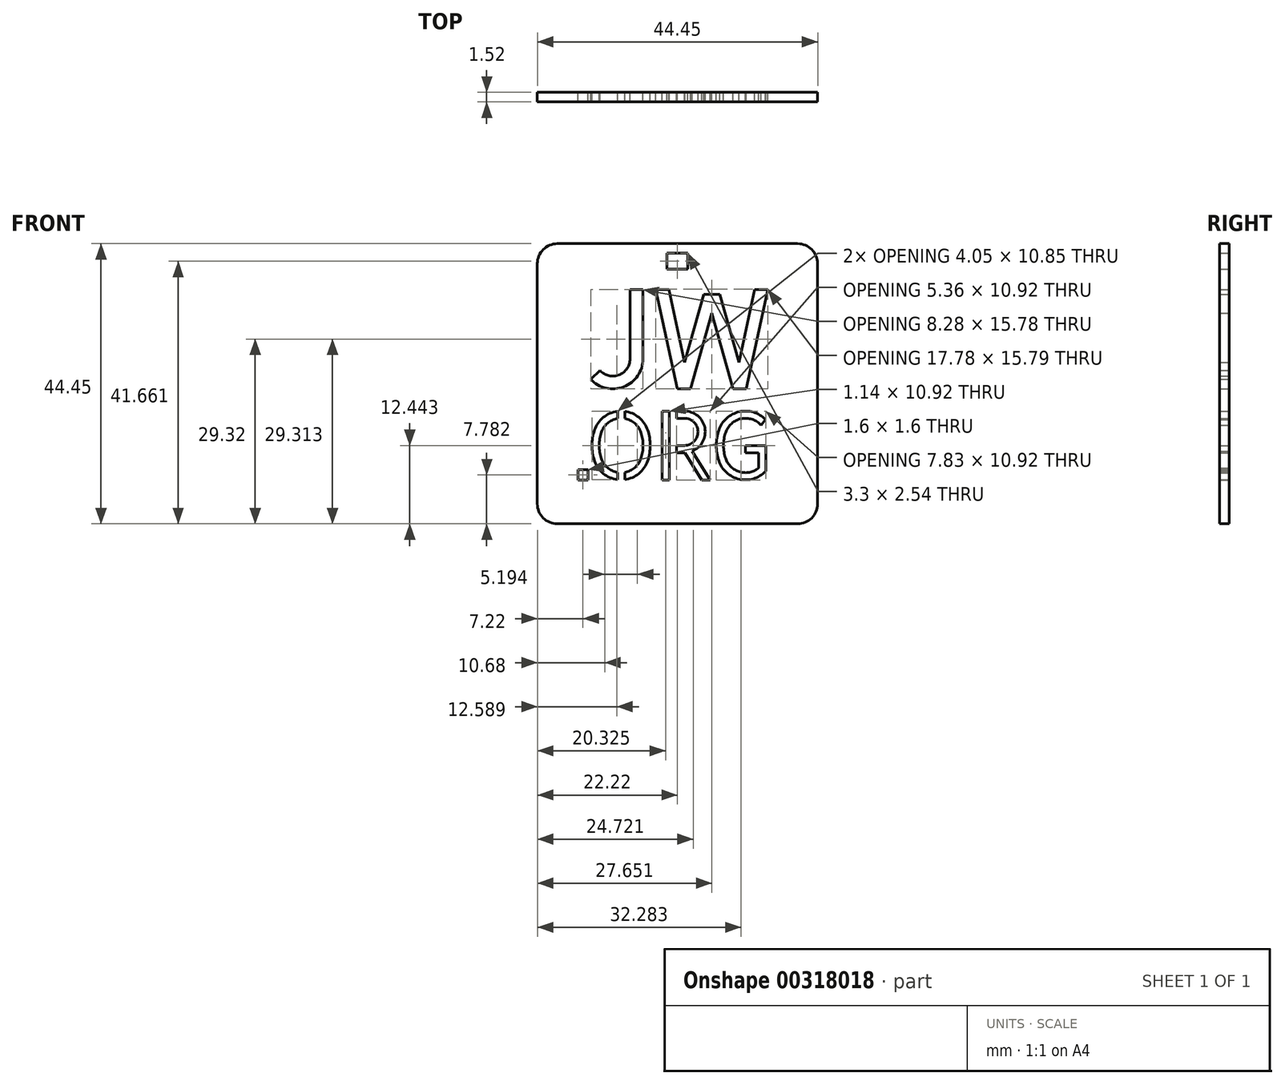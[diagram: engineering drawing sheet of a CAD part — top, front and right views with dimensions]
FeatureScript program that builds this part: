
annotation { "Feature Type Name" : "Feature", "Feature Type Description" : "" }
export const myFeature = defineFeature(function(context is Context, id is Id, definition is map)
    precondition{}
    {
        {
            var Q0;
            Q0=qCreatedBy(makeId("Front.planeOp"),FACE);
            var sketch = newSketch(context, id + "F0", { "sketchPlane" : qUnion([Q0])});
            skPoint(sketch, "E0.0", {"position": v(0, 0) * mm});
            skArc(sketch, "E1.0", {"start": v(-37.67, 27.5) * mm, "mid": v(-34.67, 26.8) * mm, "end": v(-32.92, 29.36) * mm});
            skLineSegment(sketch, "E2.0", {"start": v(-39.17, 26.13) * mm, "end": v(-37.67, 27.5) * mm});
            skArc(sketch, "E3.0", {"start": v(-39.17, 26.13) * mm, "mid": v(-33.93, 24.91) * mm, "end": v(-30.9, 29.36) * mm});
            skLineSegment(sketch, "E4.0", {"start": v(-30.9, 29.36) * mm, "end": v(-30.9, 40.38) * mm});
            skLineSegment(sketch, "E5.0", {"start": v(-32.92, 40.38) * mm, "end": v(-32.92, 29.36) * mm});
            skPoint(sketch, "E6.0", {"position": v(-31.9, 40.38) * mm});
            skPoint(sketch, "E7.0", {"position": v(-27.82, 40.38) * mm});
            skLineSegment(sketch, "E8.0", {"start": v(-21.24, 39.62) * mm, "end": v(-18.7, 39.62) * mm});
            skPoint(sketch, "E9.0", {"position": v(-12.12, 40.38) * mm});
            skLineSegment(sketch, "E10.0", {"start": v(-13.16, 40.38) * mm, "end": v(-11.08, 40.38) * mm});
            skLineSegment(sketch, "E11.0", {"start": v(-28.86, 40.38) * mm, "end": v(-26.78, 40.38) * mm});
            skLineSegment(sketch, "E12.0", {"start": v(-30.9, 40.38) * mm, "end": v(-32.92, 40.38) * mm});
            skLineSegment(sketch, "E13.0", {"start": v(-28.86, 40.38) * mm, "end": v(-25.45, 24.59) * mm});
            skLineSegment(sketch, "E14.0", {"start": v(-26.78, 40.38) * mm, "end": v(-24.28, 28.8) * mm});
            skLineSegment(sketch, "E15.0", {"start": v(-21.24, 39.62) * mm, "end": v(-24.28, 28.8) * mm});
            skLineSegment(sketch, "E16.0", {"start": v(-15.65, 28.8) * mm, "end": v(-18.7, 39.62) * mm});
            skLineSegment(sketch, "E17.0", {"start": v(-15.65, 28.8) * mm, "end": v(-13.16, 40.38) * mm});
            skLineSegment(sketch, "E18.0", {"start": v(-14.48, 24.59) * mm, "end": v(-11.08, 40.38) * mm});
            skLineSegment(sketch, "E19.0", {"start": v(-16.58, 24.59) * mm, "end": v(-14.48, 24.59) * mm});
            skLineSegment(sketch, "E20.0", {"start": v(-16.58, 24.59) * mm, "end": v(-19.97, 36.63) * mm});
            skLineSegment(sketch, "E21.0", {"start": v(-19.97, 36.63) * mm, "end": v(-23.36, 24.59) * mm});
            skLineSegment(sketch, "E22.0", {"start": v(-25.45, 24.59) * mm, "end": v(-23.36, 24.59) * mm});
            skPoint(sketch, "E23", {"position": v(-40.4, 10.95) * mm});
            skPoint(sketch, "E24", {"position": v(-27.87, 10.15) * mm});
            skPoint(sketch, "E25", {"position": v(-34.34, 10.15) * mm});
            skPoint(sketch, "E26", {"position": v(-14.63, 10.15) * mm});
            skLineSegment(sketch, "E27.bottom", {"start": v(-39.6, 11.75) * mm, "end": v(-41.2, 11.75) * mm});
            skLineSegment(sketch, "E27.top", {"start": v(-39.6, 10.15) * mm, "end": v(-41.2, 10.15) * mm});
            skLineSegment(sketch, "E27.left", {"start": v(-39.6, 11.75) * mm, "end": v(-39.6, 10.15) * mm});
            skLineSegment(sketch, "E27.right", {"start": v(-41.2, 11.75) * mm, "end": v(-41.2, 10.15) * mm});
            skArc(sketch, "E28.0", {"start": v(-34.91, 19.88) * mm, "mid": v(-36.5, 19.13) * mm, "end": v(-37.48, 17.68) * mm});
            skArc(sketch, "E28.1", {"start": v(-37.48, 13.55) * mm, "mid": v(-36.5, 12.1) * mm, "end": v(-34.91, 11.34) * mm});
            skArc(sketch, "E28.2", {"start": v(-38.57, 13.18) * mm, "mid": v(-37.17, 11.16) * mm, "end": v(-34.91, 10.19) * mm});
            skArc(sketch, "E28.3", {"start": v(-34.91, 19.88) * mm, "mid": v(-36.5, 19.13) * mm, "end": v(-37.48, 17.68) * mm});
            skArc(sketch, "E28.4", {"start": v(-34.91, 21.04) * mm, "mid": v(-37.17, 20.06) * mm, "end": v(-38.57, 18.04) * mm});
            skArc(sketch, "E28.5", {"start": v(-37.48, 13.55) * mm, "mid": v(-36.5, 12.1) * mm, "end": v(-34.91, 11.34) * mm});
            skArc(sketch, "E28.6", {"start": v(-37.48, 17.68) * mm, "mid": v(-37.82, 15.61) * mm, "end": v(-37.48, 13.55) * mm});
            skArc(sketch, "E28.7", {"start": v(-38.57, 18.04) * mm, "mid": v(-38.97, 15.61) * mm, "end": v(-38.57, 13.18) * mm});
            skArc(sketch, "E28.8", {"start": v(-33.77, 11.34) * mm, "mid": v(-32.19, 12.1) * mm, "end": v(-31.2, 13.55) * mm});
            skArc(sketch, "E28.9", {"start": v(-30.12, 13.18) * mm, "mid": v(-29.72, 15.61) * mm, "end": v(-30.12, 18.04) * mm});
            skArc(sketch, "E28.10", {"start": v(-30.12, 18.04) * mm, "mid": v(-31.52, 20.06) * mm, "end": v(-33.77, 21.04) * mm});
            skArc(sketch, "E28.11", {"start": v(-31.2, 17.68) * mm, "mid": v(-32.19, 19.13) * mm, "end": v(-33.77, 19.88) * mm});
            skArc(sketch, "E28.12", {"start": v(-30.12, 18.04) * mm, "mid": v(-31.52, 20.06) * mm, "end": v(-33.77, 21.04) * mm});
            skArc(sketch, "E28.13", {"start": v(-31.2, 13.55) * mm, "mid": v(-30.86, 15.61) * mm, "end": v(-31.2, 17.68) * mm});
            skArc(sketch, "E28.14", {"start": v(-33.77, 10.19) * mm, "mid": v(-31.52, 11.16) * mm, "end": v(-30.12, 13.18) * mm});
            skArc(sketch, "E28.15", {"start": v(-33.77, 10.19) * mm, "mid": v(-31.52, 11.16) * mm, "end": v(-30.12, 13.18) * mm});
            skLineSegment(sketch, "E29.0", {"start": v(-34.91, 21.04) * mm, "end": v(-34.91, 19.88) * mm});
            skLineSegment(sketch, "E30.0", {"start": v(-33.77, 21.04) * mm, "end": v(-33.77, 19.88) * mm});
            skLineSegment(sketch, "E31.0", {"start": v(-34.91, 11.34) * mm, "end": v(-34.91, 10.19) * mm});
            skLineSegment(sketch, "E32.0", {"start": v(-33.77, 11.34) * mm, "end": v(-33.77, 10.19) * mm});
            skLineSegment(sketch, "E33.0.0", {"start": v(-26.72, 21.07) * mm, "end": v(-26.72, 10.15) * mm});
            skLineSegment(sketch, "E33.0.1", {"start": v(-26.72, 21.07) * mm, "end": v(-27.87, 21.07) * mm});
            skLineSegment(sketch, "E33.0.2", {"start": v(-27.87, 21.07) * mm, "end": v(-27.87, 10.15) * mm});
            skLineSegment(sketch, "E33.0.3", {"start": v(-27.87, 10.15) * mm, "end": v(-26.72, 10.15) * mm});
            skLineSegment(sketch, "E34.0.0", {"start": v(-24.3, 21.07) * mm, "end": v(-25.58, 21.07) * mm});
            skLineSegment(sketch, "E34.0.1", {"start": v(-25.58, 21.07) * mm, "end": v(-25.58, 19.93) * mm});
            skLineSegment(sketch, "E34.0.2", {"start": v(-25.58, 19.93) * mm, "end": v(-24.3, 19.93) * mm});
            skArc(sketch, "E34.0.3", {"start": v(-24.3, 19.93) * mm, "mid": v(-22.15, 17.8) * mm, "end": v(-24.26, 15.61) * mm});
            skLineSegment(sketch, "E34.0.4", {"start": v(-24.26, 15.61) * mm, "end": v(-25.58, 15.61) * mm});
            skLineSegment(sketch, "E34.0.5", {"start": v(-25.58, 15.61) * mm, "end": v(-25.58, 14.47) * mm});
            skFitSpline(sketch, "E34.0.6", {"points": [v(-26.72, 14.47) * mm, v(-25.9, 14.47) * mm, v(-25.08, 14.47) * mm, v(-24.25, 14.47) * mm]});
            skLineSegment(sketch, "E34.0.7", {"start": v(-24.25, 14.47) * mm, "end": v(-21.56, 10.15) * mm});
            skLineSegment(sketch, "E34.0.8", {"start": v(-21.56, 10.15) * mm, "end": v(-20.22, 10.15) * mm});
            skLineSegment(sketch, "E34.0.9", {"start": v(-20.22, 10.15) * mm, "end": v(-23.06, 14.72) * mm});
            skArc(sketch, "E34.0.10", {"start": v(-23.06, 14.72) * mm, "mid": v(-21.07, 18.4) * mm, "end": v(-24.3, 21.07) * mm});
            skArc(sketch, "E35.0.0", {"start": v(-17.77, 17.68) * mm, "mid": v(-15.28, 19.87) * mm, "end": v(-12.14, 18.8) * mm});
            skLineSegment(sketch, "E35.0.1", {"start": v(-12.14, 18.8) * mm, "end": v(-11.43, 19.72) * mm});
            skArc(sketch, "E35.0.2", {"start": v(-11.43, 19.72) * mm, "mid": v(-15.61, 20.96) * mm, "end": v(-18.85, 18.04) * mm});
            skArc(sketch, "E35.0.3", {"start": v(-18.85, 18.04) * mm, "mid": v(-19.25, 15.61) * mm, "end": v(-18.85, 13.18) * mm});
            skArc(sketch, "E35.0.4", {"start": v(-18.85, 13.18) * mm, "mid": v(-15.6, 10.26) * mm, "end": v(-11.42, 11.5) * mm});
            skLineSegment(sketch, "E35.0.5", {"start": v(-11.42, 11.5) * mm, "end": v(-11.42, 15.61) * mm});
            skLineSegment(sketch, "E35.0.6", {"start": v(-11.42, 15.61) * mm, "end": v(-14.63, 15.61) * mm});
            skLineSegment(sketch, "E35.0.7", {"start": v(-14.63, 15.61) * mm, "end": v(-14.63, 14.47) * mm});
            skLineSegment(sketch, "E35.0.8", {"start": v(-14.63, 14.47) * mm, "end": v(-12.57, 14.47) * mm});
            skLineSegment(sketch, "E35.0.9", {"start": v(-12.57, 14.47) * mm, "end": v(-12.57, 12.01) * mm});
            skArc(sketch, "E35.0.10", {"start": v(-12.57, 12.01) * mm, "mid": v(-15.57, 11.43) * mm, "end": v(-17.77, 13.55) * mm});
            skArc(sketch, "E35.0.11", {"start": v(-17.77, 13.55) * mm, "mid": v(-18.1, 15.61) * mm, "end": v(-17.77, 17.68) * mm});
            skSolve(sketch);
        }
        {
            var Q0;
            Q0=qCreatedBy(makeId("Front.planeOp"),FACE);
            var sketch = newSketch(context, id + "F1", { "sketchPlane" : qUnion([Q0])});
            skLineSegment(sketch, "E36.bottom", {"start": v(0, 0) * mm, "end": v(-50.8, 0) * mm});
            skLineSegment(sketch, "E36.top", {"start": v(0, 50.8) * mm, "end": v(-50.8, 50.8) * mm});
            skLineSegment(sketch, "E36.left", {"start": v(0, 0) * mm, "end": v(0, 50.8) * mm});
            skLineSegment(sketch, "E36.right", {"start": v(-50.8, 0) * mm, "end": v(-50.8, 50.8) * mm});
            skLineSegment(sketch, "E37.0", {"start": v(-3.18, 47.63) * mm, "end": v(-47.63, 47.63) * mm});
            skLineSegment(sketch, "E37.1", {"start": v(-3.17, 3.18) * mm, "end": v(-3.18, 47.63) * mm});
            skLineSegment(sketch, "E37.2", {"start": v(-3.17, 3.17) * mm, "end": v(-47.63, 3.17) * mm});
            skLineSegment(sketch, "E37.3", {"start": v(-47.63, 3.17) * mm, "end": v(-47.63, 47.62) * mm});
            skPoint(sketch, "E38.0", {"position": v(-41.2, 10.15) * mm});
            skPoint(sketch, "E39", {"position": v(-25.4, 25.4) * mm});
            skCircle(sketch, "E40", {"center": v(-25.4, 25.4) * mm, "radius": 25.4 * mm});
            skLineSegment(sketch, "E41.bottom", {"start": v(-23.75, 46.1) * mm, "end": v(-27.05, 46.1) * mm});
            skLineSegment(sketch, "E41.top", {"start": v(-23.75, 43.56) * mm, "end": v(-27.05, 43.56) * mm});
            skLineSegment(sketch, "E41.left", {"start": v(-23.75, 46.1) * mm, "end": v(-23.75, 43.56) * mm});
            skLineSegment(sketch, "E41.right", {"start": v(-27.05, 46.1) * mm, "end": v(-27.05, 43.56) * mm});
            skPoint(sketch, "E41.middle", {"position": v(-25.4, 44.83) * mm});
            skPoint(sketch, "E41.middle.positionSnap0", {"position": v(-25.4, 47.63) * mm});
            skPoint(sketch, "E41.centerSnap0", {"position": v(-25.4, 47.63) * mm});
            skPoint(sketch, "E42.0", {"position": v(-24.28, 28.8) * mm});
            skLineSegment(sketch, "E43.0.0", {"start": v(-30.9, 29.36) * mm, "end": v(-30.9, 40.38) * mm});
            skLineSegment(sketch, "E43.0.1", {"start": v(-30.9, 40.38) * mm, "end": v(-32.92, 40.38) * mm});
            skLineSegment(sketch, "E43.0.2", {"start": v(-32.92, 40.38) * mm, "end": v(-32.92, 29.36) * mm});
            skArc(sketch, "E43.0.3", {"start": v(-32.92, 29.36) * mm, "mid": v(-34.67, 26.8) * mm, "end": v(-37.67, 27.5) * mm});
            skLineSegment(sketch, "E43.0.4", {"start": v(-37.67, 27.5) * mm, "end": v(-39.17, 26.13) * mm});
            skArc(sketch, "E43.0.5", {"start": v(-39.17, 26.13) * mm, "mid": v(-33.93, 24.91) * mm, "end": v(-30.9, 29.36) * mm});
            skLineSegment(sketch, "E44.0.0", {"start": v(-26.78, 40.38) * mm, "end": v(-28.86, 40.38) * mm});
            skLineSegment(sketch, "E44.0.1", {"start": v(-28.86, 40.38) * mm, "end": v(-25.45, 24.59) * mm});
            skLineSegment(sketch, "E44.0.2", {"start": v(-25.45, 24.59) * mm, "end": v(-23.36, 24.59) * mm});
            skLineSegment(sketch, "E44.0.3", {"start": v(-23.36, 24.59) * mm, "end": v(-19.97, 36.63) * mm});
            skLineSegment(sketch, "E44.0.4", {"start": v(-19.97, 36.63) * mm, "end": v(-16.58, 24.59) * mm});
            skLineSegment(sketch, "E44.0.5", {"start": v(-16.58, 24.59) * mm, "end": v(-14.48, 24.59) * mm});
            skLineSegment(sketch, "E44.0.6", {"start": v(-14.48, 24.59) * mm, "end": v(-11.08, 40.38) * mm});
            skLineSegment(sketch, "E44.0.7", {"start": v(-11.08, 40.38) * mm, "end": v(-13.16, 40.38) * mm});
            skLineSegment(sketch, "E44.0.8", {"start": v(-13.16, 40.38) * mm, "end": v(-15.65, 28.8) * mm});
            skLineSegment(sketch, "E44.0.9", {"start": v(-15.65, 28.8) * mm, "end": v(-18.7, 39.62) * mm});
            skLineSegment(sketch, "E44.0.10", {"start": v(-18.7, 39.62) * mm, "end": v(-21.24, 39.62) * mm});
            skLineSegment(sketch, "E44.0.11", {"start": v(-21.24, 39.62) * mm, "end": v(-24.28, 28.8) * mm});
            skLineSegment(sketch, "E44.0.12", {"start": v(-24.28, 28.8) * mm, "end": v(-26.78, 40.38) * mm});
            skArc(sketch, "E45.0.0", {"start": v(-30.12, 13.18) * mm, "mid": v(-29.72, 15.61) * mm, "end": v(-30.12, 18.04) * mm});
            skArc(sketch, "E45.0.1", {"start": v(-30.12, 18.04) * mm, "mid": v(-31.52, 20.06) * mm, "end": v(-33.77, 21.04) * mm});
            skLineSegment(sketch, "E45.0.2", {"start": v(-33.77, 21.04) * mm, "end": v(-33.77, 19.88) * mm});
            skArc(sketch, "E45.0.3", {"start": v(-33.77, 19.88) * mm, "mid": v(-32.19, 19.13) * mm, "end": v(-31.2, 17.68) * mm});
            skArc(sketch, "E45.0.4", {"start": v(-31.2, 17.68) * mm, "mid": v(-30.86, 15.61) * mm, "end": v(-31.2, 13.55) * mm});
            skArc(sketch, "E45.0.5", {"start": v(-31.2, 13.55) * mm, "mid": v(-32.19, 12.1) * mm, "end": v(-33.77, 11.34) * mm});
            skLineSegment(sketch, "E45.0.6", {"start": v(-33.77, 11.34) * mm, "end": v(-33.77, 10.19) * mm});
            skArc(sketch, "E45.0.7", {"start": v(-33.77, 10.19) * mm, "mid": v(-31.52, 11.16) * mm, "end": v(-30.12, 13.18) * mm});
            skArc(sketch, "E46.0.0", {"start": v(-37.48, 17.68) * mm, "mid": v(-36.5, 19.13) * mm, "end": v(-34.91, 19.88) * mm});
            skLineSegment(sketch, "E46.0.1", {"start": v(-34.91, 19.88) * mm, "end": v(-34.91, 21.04) * mm});
            skArc(sketch, "E46.0.2", {"start": v(-34.91, 21.04) * mm, "mid": v(-37.17, 20.06) * mm, "end": v(-38.57, 18.04) * mm});
            skArc(sketch, "E46.0.3", {"start": v(-38.57, 18.04) * mm, "mid": v(-38.97, 15.61) * mm, "end": v(-38.57, 13.18) * mm});
            skArc(sketch, "E46.0.4", {"start": v(-38.57, 13.18) * mm, "mid": v(-37.17, 11.16) * mm, "end": v(-34.91, 10.19) * mm});
            skLineSegment(sketch, "E46.0.5", {"start": v(-34.91, 10.19) * mm, "end": v(-34.91, 11.34) * mm});
            skArc(sketch, "E46.0.6", {"start": v(-34.91, 11.34) * mm, "mid": v(-36.5, 12.1) * mm, "end": v(-37.48, 13.55) * mm});
            skArc(sketch, "E46.0.7", {"start": v(-37.48, 13.55) * mm, "mid": v(-37.82, 15.61) * mm, "end": v(-37.48, 17.68) * mm});
            skLineSegment(sketch, "E47.0.0", {"start": v(-27.87, 21.07) * mm, "end": v(-27.87, 10.15) * mm});
            skLineSegment(sketch, "E47.0.1", {"start": v(-27.87, 10.15) * mm, "end": v(-26.72, 10.15) * mm});
            skLineSegment(sketch, "E47.0.2", {"start": v(-26.72, 10.15) * mm, "end": v(-26.72, 21.07) * mm});
            skLineSegment(sketch, "E47.0.3", {"start": v(-26.72, 21.07) * mm, "end": v(-27.87, 21.07) * mm});
            skLineSegment(sketch, "E48.0.0", {"start": v(-20.22, 10.15) * mm, "end": v(-23.06, 14.72) * mm});
            skArc(sketch, "E48.0.1", {"start": v(-23.06, 14.72) * mm, "mid": v(-21.07, 18.4) * mm, "end": v(-24.3, 21.07) * mm});
            skLineSegment(sketch, "E48.0.2", {"start": v(-24.3, 21.07) * mm, "end": v(-25.58, 21.07) * mm});
            skLineSegment(sketch, "E48.0.3", {"start": v(-25.58, 21.07) * mm, "end": v(-25.58, 19.93) * mm});
            skLineSegment(sketch, "E48.0.4", {"start": v(-25.58, 19.93) * mm, "end": v(-24.3, 19.93) * mm});
            skArc(sketch, "E48.0.5", {"start": v(-24.3, 19.93) * mm, "mid": v(-22.15, 17.8) * mm, "end": v(-24.26, 15.61) * mm});
            skLineSegment(sketch, "E48.0.6", {"start": v(-24.26, 15.61) * mm, "end": v(-25.58, 15.61) * mm});
            skLineSegment(sketch, "E48.0.7", {"start": v(-25.58, 15.61) * mm, "end": v(-25.58, 14.47) * mm});
            skFitSpline(sketch, "E48.0.8", {"points": [v(-26.72, 14.47) * mm, v(-25.9, 14.47) * mm, v(-25.08, 14.47) * mm, v(-24.25, 14.47) * mm]});
            skLineSegment(sketch, "E48.0.9", {"start": v(-24.25, 14.47) * mm, "end": v(-21.56, 10.15) * mm});
            skLineSegment(sketch, "E48.0.10", {"start": v(-21.56, 10.15) * mm, "end": v(-20.22, 10.15) * mm});
            skArc(sketch, "E49.0.0", {"start": v(-12.57, 12.01) * mm, "mid": v(-15.57, 11.43) * mm, "end": v(-17.77, 13.55) * mm});
            skArc(sketch, "E49.0.1", {"start": v(-17.77, 13.55) * mm, "mid": v(-18.1, 15.61) * mm, "end": v(-17.77, 17.68) * mm});
            skArc(sketch, "E49.0.2", {"start": v(-17.77, 17.68) * mm, "mid": v(-15.28, 19.87) * mm, "end": v(-12.14, 18.8) * mm});
            skLineSegment(sketch, "E49.0.3", {"start": v(-12.14, 18.8) * mm, "end": v(-11.43, 19.72) * mm});
            skArc(sketch, "E49.0.4", {"start": v(-11.43, 19.72) * mm, "mid": v(-15.61, 20.96) * mm, "end": v(-18.85, 18.04) * mm});
            skArc(sketch, "E49.0.5", {"start": v(-18.85, 18.04) * mm, "mid": v(-19.25, 15.61) * mm, "end": v(-18.85, 13.18) * mm});
            skArc(sketch, "E49.0.6", {"start": v(-18.85, 13.18) * mm, "mid": v(-15.6, 10.26) * mm, "end": v(-11.42, 11.5) * mm});
            skLineSegment(sketch, "E49.0.7", {"start": v(-11.42, 11.5) * mm, "end": v(-11.42, 15.61) * mm});
            skLineSegment(sketch, "E49.0.8", {"start": v(-11.42, 15.61) * mm, "end": v(-14.63, 15.61) * mm});
            skLineSegment(sketch, "E49.0.9", {"start": v(-14.63, 15.61) * mm, "end": v(-14.63, 14.47) * mm});
            skLineSegment(sketch, "E49.0.10", {"start": v(-14.63, 14.47) * mm, "end": v(-12.57, 14.47) * mm});
            skLineSegment(sketch, "E49.0.11", {"start": v(-12.57, 14.47) * mm, "end": v(-12.57, 12.01) * mm});
            skLineSegment(sketch, "E50.0.0", {"start": v(-41.2, 10.15) * mm, "end": v(-39.6, 10.15) * mm});
            skLineSegment(sketch, "E50.0.1", {"start": v(-39.6, 10.15) * mm, "end": v(-39.6, 11.75) * mm});
            skLineSegment(sketch, "E50.0.2", {"start": v(-39.6, 11.75) * mm, "end": v(-41.2, 11.75) * mm});
            skLineSegment(sketch, "E50.0.3", {"start": v(-41.2, 11.75) * mm, "end": v(-41.2, 10.15) * mm});
            skPoint(sketch, "E51.0", {"position": v(-40.4, 10.95) * mm});
            skSolve(sketch);
        }
        {
            var Q0;
            {var subQ0=sQuery(id+"F1.wireOp",EDGE,"E37.1");var subQ1=sQuery(id+"F1.wireOp",EDGE,"E37.0");var subQ2=makeQuery(id+"F1.imprint","INTERSECT",VERTEX,{"derivedFrom":[subQ1,subQ0]});Q0=makeQuery(id+"F1.imprint","IMPRINT",FACE,{"disambiguationData":[TD([[makeQuery(id+"F1.imprint","IMPRINT",EDGE,{"disambiguationData":[TD([[subQ2,-1.0]])],"derivedFrom":subQ1}),1.0]])]});}
            var Q1;
            Q1=makeQuery(id+"F1.imprint","IMPRINT",FACE,{"disambiguationData":[TD([[makeQuery(id+"F1.imprint","IMPRINT",EDGE,{"derivedFrom":sQuery(id+"F1.wireOp",EDGE,"E41.bottom")}),-1.0]])]});
            var Q2;
            {var subQ0=sQuery(id+"F1.wireOp",EDGE,"E37.2");var subQ1=sQuery(id+"F1.wireOp",EDGE,"E37.1");var subQ2=makeQuery(id+"F1.imprint","INTERSECT",VERTEX,{"derivedFrom":[subQ1,subQ0]});Q2=makeQuery(id+"F1.imprint","IMPRINT",FACE,{"disambiguationData":[TD([[makeQuery(id+"F1.imprint","IMPRINT",EDGE,{"disambiguationData":[TD([[subQ2,-1.0]])],"derivedFrom":subQ1}),1.0]])]});}
            var Q3;
            {var subQ0=sQuery(id+"F1.wireOp",EDGE,"E37.3");var subQ1=sQuery(id+"F1.wireOp",EDGE,"E37.0");var subQ2=makeQuery(id+"F1.imprint","INTERSECT",VERTEX,{"derivedFrom":[subQ1,subQ0]});Q3=makeQuery(id+"F1.imprint","IMPRINT",FACE,{"disambiguationData":[TD([[makeQuery(id+"F1.imprint","IMPRINT",EDGE,{"disambiguationData":[TD([[subQ2,1.0]])],"derivedFrom":subQ1}),1.0]])]});}
            var Q4;
            {var subQ0=sQuery(id+"F1.wireOp",EDGE,"E37.3");var subQ1=sQuery(id+"F1.wireOp",EDGE,"E37.2");var subQ2=makeQuery(id+"F1.imprint","INTERSECT",VERTEX,{"derivedFrom":[subQ1,subQ0]});Q4=makeQuery(id+"F1.imprint","IMPRINT",FACE,{"disambiguationData":[TD([[makeQuery(id+"F1.imprint","IMPRINT",EDGE,{"disambiguationData":[TD([[subQ2,1.0]])],"derivedFrom":subQ1}),-1.0]])]});}
            extrude(context, id + "F2", {"entities" : qUnion([Q0, Q1, Q2, Q3, Q4]), "depth" : 1.52 * mm});
        }
        {
            var Q0;
            Q0=makeQuery(id+"F2.opExtrude","SWEPT_EDGE",EDGE,{"disambiguationData":[OSD([sQuery(id+"F1.wireOp",EDGE,"E37.0"),sQuery(id+"F1.wireOp",EDGE,"E37.3")])]});
            var Q1;
            Q1=makeQuery(id+"F2.opExtrude","SWEPT_EDGE",EDGE,{"disambiguationData":[OSD([sQuery(id+"F1.wireOp",EDGE,"E37.0"),sQuery(id+"F1.wireOp",EDGE,"E37.1")])]});
            var Q2;
            Q2=makeQuery(id+"F2.opExtrude","SWEPT_EDGE",EDGE,{"disambiguationData":[OSD([sQuery(id+"F1.wireOp",EDGE,"E37.1"),sQuery(id+"F1.wireOp",EDGE,"E37.2")])]});
            var Q3;
            Q3=makeQuery(id+"F2.opExtrude","SWEPT_EDGE",EDGE,{"disambiguationData":[OSD([sQuery(id+"F1.wireOp",EDGE,"E37.2"),sQuery(id+"F1.wireOp",EDGE,"E37.3")])]});
            fillet(context, id + "F3", {"entities" : qUnion([Q0, Q1, Q2, Q3]), "radius" : 3.17 * mm, "tangentPropagation" : true, "allowEdgeOverflow" : false});
        }
    });
